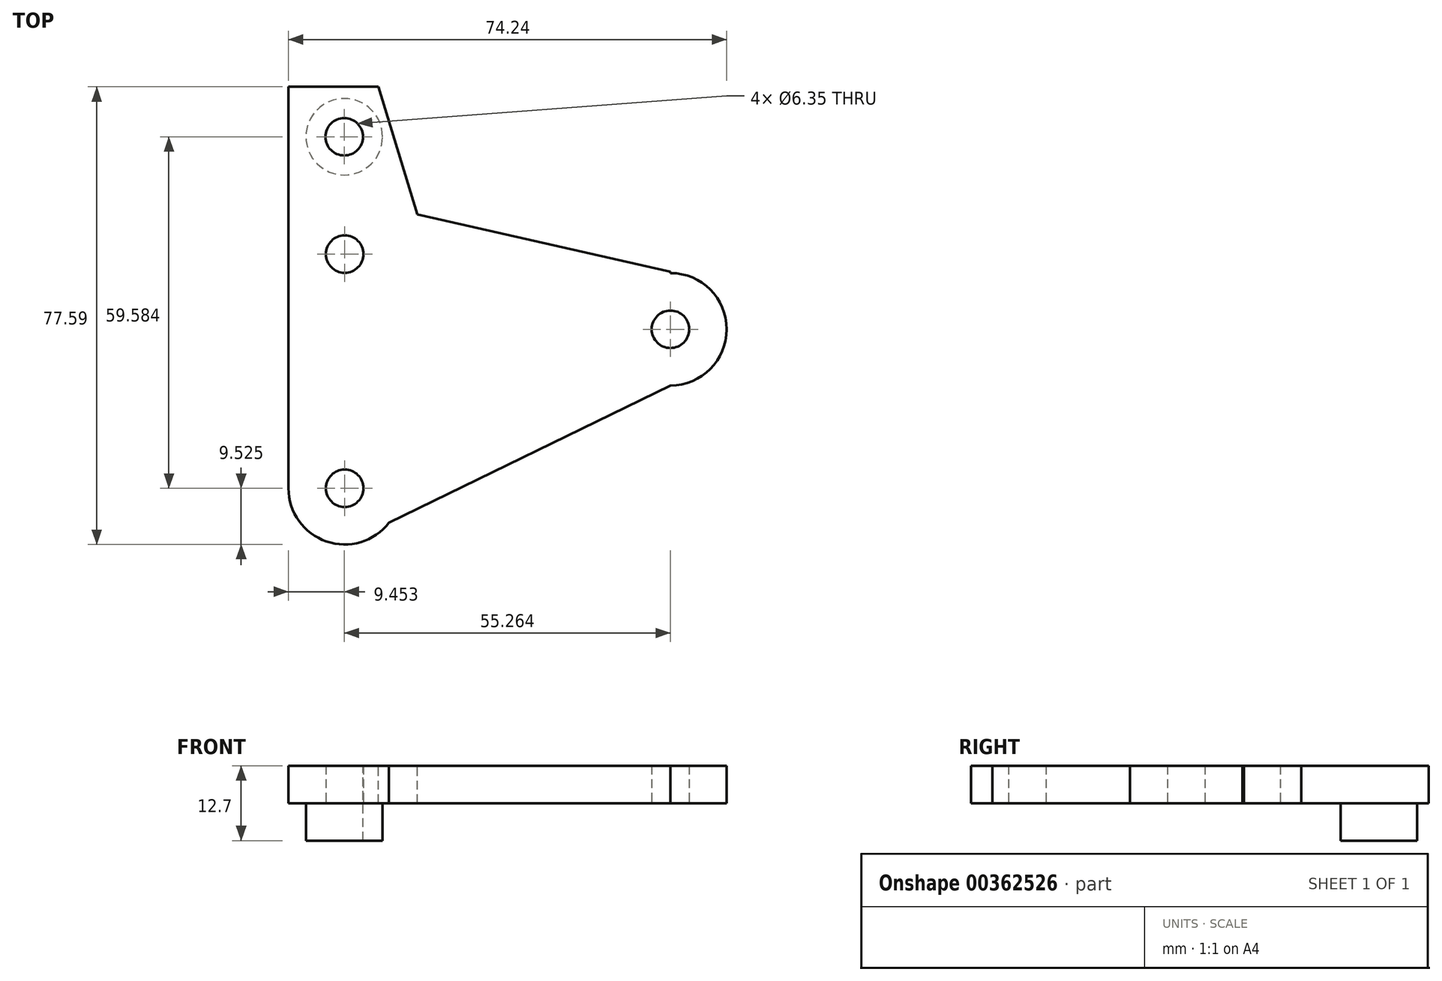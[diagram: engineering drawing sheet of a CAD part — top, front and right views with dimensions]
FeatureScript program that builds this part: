
annotation { "Feature Type Name" : "Feature", "Feature Type Description" : "" }
export const myFeature = defineFeature(function(context is Context, id is Id, definition is map)
    precondition{}
    {
        {
            var Q0;
            Q0=qCreatedBy(makeId("Top.planeOp"),FACE);
            var sketch = newSketch(context, id + "F0", { "sketchPlane" : qUnion([Q0])});
            skLineSegment(sketch, "E0", {"start": v(0, 0) * mm, "end": v(0, 12.74) * mm});
            skLineSegment(sketch, "E1", {"start": v(0, 0) * mm, "end": v(55.19, 0) * mm});
            skLineSegment(sketch, "E2", {"start": v(0, 0) * mm, "end": v(0, -26.96) * mm});
            skLineSegment(sketch, "E3", {"start": v(0, 12.74) * mm, "end": v(55.19, 0) * mm});
            skLineSegment(sketch, "E4", {"start": v(0, -26.96) * mm, "end": v(55.19, 0) * mm});
            skCircle(sketch, "E5", {"center": v(0, 12.74) * mm, "radius": 3.18 * mm});
            skCircle(sketch, "E6", {"center": v(55.19, 0) * mm, "radius": 3.18 * mm});
            skCircle(sketch, "E7", {"center": v(0, -26.96) * mm, "radius": 3.18 * mm});
            skCircle(sketch, "E8", {"center": v(0, -26.96) * mm, "radius": 9.53 * mm});
            skCircle(sketch, "E9", {"center": v(55.19, 0) * mm, "radius": 9.53 * mm});
            skCircle(sketch, "E10", {"center": v(0, 12.74) * mm, "radius": 9.53 * mm});
            skLineSegment(sketch, "E11", {"start": v(-9.53, 12.74) * mm, "end": v(-9.53, -26.96) * mm});
            skLineSegment(sketch, "E12", {"start": v(0, 12.74) * mm, "end": v(0, 22.27) * mm});
            skLineSegment(sketch, "E13", {"start": v(0, 22.27) * mm, "end": v(55.19, 9.77) * mm});
            skLineSegment(sketch, "E14", {"start": v(55.19, 9.77) * mm, "end": v(55.19, 0) * mm});
            skLineSegment(sketch, "E15", {"start": v(55.19, -9.52) * mm, "end": v(0, -36.48) * mm});
            skSolve(sketch);
        }
        {
            var Q0;
            Q0 = qSketchRegion(id + "F0", true);
            var Q1;
            {var subQ3=sQuery(id+"F0.wireOp",EDGE,"E3");var subQ5=sQuery(id+"F0.wireOp",EDGE,"E10");var subQ6=makeQuery(id+"F0.imprint","INTERSECT",VERTEX,{"derivedFrom":[subQ3,subQ5]});Q1=makeQuery(id+"F0.imprint","IMPRINT",FACE,{"disambiguationData":[TD([[makeQuery(id+"F0.imprint","IMPRINT",EDGE,{"disambiguationData":[TD([[subQ6,-1.0]])],"derivedFrom":subQ3}),-1.0]])]});}
            var Q2;
            {var subQ0=sQuery(id+"F0.wireOp",EDGE,"E10");var subQ1=sQuery(id+"F0.wireOp",EDGE,"E0");var subQ2=makeQuery(id+"F0.imprint","INTERSECT",VERTEX,{"derivedFrom":[subQ1,subQ0]});Q2=makeQuery(id+"F0.imprint","IMPRINT",FACE,{"disambiguationData":[TD([[makeQuery(id+"F0.imprint","IMPRINT",EDGE,{"disambiguationData":[TD([[subQ2,-1.0]])],"derivedFrom":subQ1}),-1.0]])]});}
            var Q3;
            {var subQ0=sQuery(id+"F0.wireOp",EDGE,"E8");var subQ1=sQuery(id+"F0.wireOp",EDGE,"E4");var subQ2=makeQuery(id+"F0.imprint","INTERSECT",VERTEX,{"derivedFrom":[subQ1,subQ0]});Q3=makeQuery(id+"F0.imprint","IMPRINT",FACE,{"disambiguationData":[TD([[makeQuery(id+"F0.imprint","IMPRINT",EDGE,{"disambiguationData":[TD([[subQ2,-1.0]])],"derivedFrom":subQ1}),1.0]])]});}
            var Q4;
            {var subQ0=sQuery(id+"F0.wireOp",EDGE,"E8");var subQ1=sQuery(id+"F0.wireOp",EDGE,"E2");var subQ2=makeQuery(id+"F0.imprint","INTERSECT",VERTEX,{"derivedFrom":[subQ1,subQ0]});Q4=makeQuery(id+"F0.imprint","IMPRINT",FACE,{"disambiguationData":[TD([[makeQuery(id+"F0.imprint","IMPRINT",EDGE,{"disambiguationData":[TD([[subQ2,-1.0]])],"derivedFrom":subQ1}),1.0]])]});}
            var Q5;
            {var subQ0=sQuery(id+"F0.wireOp",EDGE,"E9");var subQ1=sQuery(id+"F0.wireOp",EDGE,"E1");var subQ2=makeQuery(id+"F0.imprint","INTERSECT",VERTEX,{"derivedFrom":[subQ1,subQ0]});Q5=makeQuery(id+"F0.imprint","IMPRINT",FACE,{"disambiguationData":[TD([[makeQuery(id+"F0.imprint","IMPRINT",EDGE,{"disambiguationData":[TD([[subQ2,-1.0]])],"derivedFrom":subQ1}),-1.0]])]});}
            var Q6;
            {var subQ0=sQuery(id+"F0.wireOp",EDGE,"E9");var subQ1=sQuery(id+"F0.wireOp",EDGE,"E1");var subQ2=makeQuery(id+"F0.imprint","INTERSECT",VERTEX,{"derivedFrom":[subQ1,subQ0]});Q6=makeQuery(id+"F0.imprint","IMPRINT",FACE,{"disambiguationData":[TD([[makeQuery(id+"F0.imprint","IMPRINT",EDGE,{"disambiguationData":[TD([[subQ2,-1.0]])],"derivedFrom":subQ1}),1.0]])]});}
            extrude(context, id + "F1", {"entities" : qUnion([Q0, Q1, Q2, Q3, Q4, Q5, Q6]), "depth" : 6.35 * mm});
        }
        {
            var Q0;
            Q0=makeQuery(id+"F1.opExtrude","CAP_FACE",FACE,{"disambiguationData":[OSD([sQuery(id+"F0.wireOp",EDGE,"E5"),sQuery(id+"F0.wireOp",EDGE,"E6"),sQuery(id+"F0.wireOp",EDGE,"E7"),sQuery(id+"F0.wireOp",EDGE,"E8"),sQuery(id+"F0.wireOp",EDGE,"E9"),sQuery(id+"F0.wireOp",EDGE,"E10"),sQuery(id+"F0.wireOp",EDGE,"E11"),sQuery(id+"F0.wireOp",EDGE,"E13"),sQuery(id+"F0.wireOp",EDGE,"E14"),sQuery(id+"F0.wireOp",EDGE,"E15")])],"isStart":false});
            var sketch = newSketch(context, id + "F2", { "sketchPlane" : qUnion([Q0])});
            skCircle(sketch, "E16", {"center": v(-0.08, 32.63) * mm, "radius": 3.18 * mm});
            skLineSegment(sketch, "E17", {"start": v(-9.53, 12.74) * mm, "end": v(-9.53, 41.11) * mm});
            skLineSegment(sketch, "E18", {"start": v(-9.53, 41.11) * mm, "end": v(5.72, 41.11) * mm});
            skLineSegment(sketch, "E19", {"start": v(5.72, 41.11) * mm, "end": v(12.32, 19.48) * mm});
            skLineSegment(sketch, "E20", {"start": v(12.32, 19.48) * mm, "end": v(-4.8, 16.78) * mm});
            skLineSegment(sketch, "E21", {"start": v(-4.8, 16.78) * mm, "end": v(-9.53, 12.74) * mm});
            skSolve(sketch);
        }
        {
            var Q0;
            Q0=makeQuery(id+"F2.imprint","IMPRINT",FACE,{"disambiguationData":[TD([[makeQuery(id+"F2.imprint","IMPRINT",EDGE,{"derivedFrom":sQuery(id+"F2.wireOp",EDGE,"E16")}),-1.0]])]});
            extrude(context, id + "F3", {"entities" : qUnion([Q0]), "operationType" : NewBodyOperationType.ADD, "oppositeDirection" : true, "depth" : 12.7 * mm});
        }
        {
            var Q0;
            Q0=makeQuery(id+"F3.opExtrude","CAP_FACE",FACE,{"disambiguationData":[OSD([sQuery(id+"F0.wireOp",EDGE,"E10"),sQuery(id+"F0.wireOp",EDGE,"E13"),sQuery(id+"F2.wireOp",EDGE,"E16"),sQuery(id+"F2.wireOp",EDGE,"E17"),sQuery(id+"F2.wireOp",EDGE,"E18"),sQuery(id+"F2.wireOp",EDGE,"E19")])],"isStart":false});
            var sketch = newSketch(context, id + "F4", { "sketchPlane" : qUnion([Q0])});
            skCircle(sketch, "E22", {"center": v(-0.08, -32.63) * mm, "radius": 6.48 * mm});
            skLineSegment(sketch, "E23", {"start": v(-22.7, -5.18) * mm, "end": v(28.05, -10.99) * mm});
            skLineSegment(sketch, "E24", {"start": v(28.05, -10.99) * mm, "end": v(22.35, -32.25) * mm});
            skLineSegment(sketch, "E25", {"start": v(22.35, -32.25) * mm, "end": v(-2.31, -53.08) * mm});
            skLineSegment(sketch, "E26", {"start": v(-2.31, -53.08) * mm, "end": v(-30.05, -35.98) * mm});
            skLineSegment(sketch, "E27", {"start": v(-30.05, -35.98) * mm, "end": v(-22.7, -5.18) * mm});
            skSolve(sketch);
        }
        {
            var Q0;
            Q0=makeQuery(id+"F4.imprint","IMPRINT",FACE,{"disambiguationData":[TD([[makeQuery(id+"F4.imprint","IMPRINT",EDGE,{"derivedFrom":sQuery(id+"F4.wireOp",EDGE,"E22")}),-1.0]])]});
            extrude(context, id + "F5", {"entities" : qUnion([Q0]), "operationType" : NewBodyOperationType.REMOVE, "oppositeDirection" : true, "depth" : 6.35 * mm});
        }
    });
